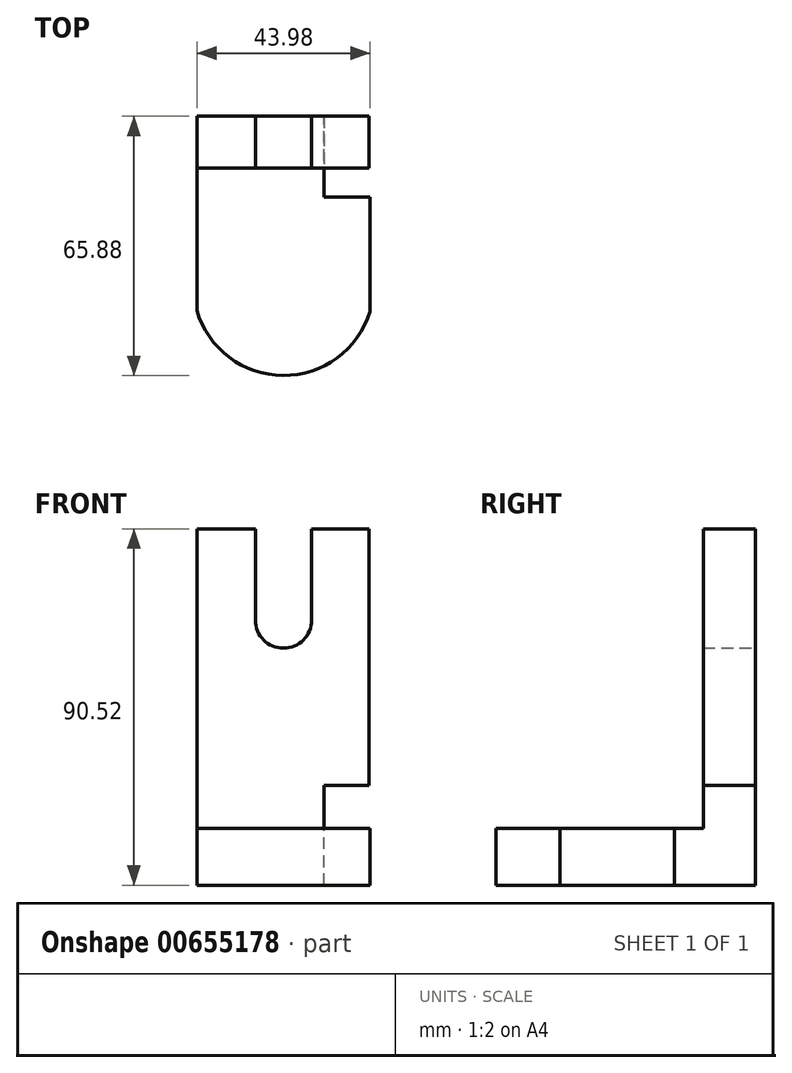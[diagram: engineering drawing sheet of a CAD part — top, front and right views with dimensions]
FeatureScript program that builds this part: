
annotation { "Feature Type Name" : "Feature", "Feature Type Description" : "" }
export const myFeature = defineFeature(function(context is Context, id is Id, definition is map)
    precondition{}
    {
        {
            var Q0;
            Q0=qCreatedBy(makeId("Front.planeOp"),FACE);
            var sketch = newSketch(context, id + "F0", { "sketchPlane" : qUnion([Q0])});
            skLineSegment(sketch, "E0.bottom", {"start": v(-21.85, 45.26) * mm, "end": v(-7, 45.26) * mm});
            skLineSegment(sketch, "E0.top", {"start": v(-21.85, -45.26) * mm, "end": v(21.85, -45.26) * mm});
            skLineSegment(sketch, "E0.left", {"start": v(-21.85, 45.26) * mm, "end": v(-21.85, -45.26) * mm});
            skLineSegment(sketch, "E0.right", {"start": v(21.85, 45.26) * mm, "end": v(21.85, -45.26) * mm});
            skPoint(sketch, "E0.middle", {"position": v(0, 0) * mm});
            skLineSegment(sketch, "E1.left", {"start": v(-7, 45.26) * mm, "end": v(-7, 22.13) * mm});
            skLineSegment(sketch, "E1.right", {"start": v(7.28, 45.26) * mm, "end": v(7.28, 22.13) * mm});
            skArc(sketch, "E2", {"start": v(-7, 22.13) * mm, "mid": v(0.14, 15) * mm, "end": v(7.28, 22.13) * mm});
            skLineSegment(sketch, "E3.trimOffspring", {"start": v(7.28, 45.26) * mm, "end": v(21.85, 45.26) * mm});
            skSolve(sketch);
        }
        {
            var Q0;
            Q0 = qSketchRegion(id + "F0", true);
            extrude(context, id + "F1", {"entities" : qUnion([Q0]), "depth" : 13.2 * mm, "offsetDistance" : 25.4 * mm});
        }
        {
            var Q0;
            Q0=makeQuery(id+"F1.opExtrude","CAP_FACE",FACE,{"disambiguationData":[OSD([sQuery(id+"F0.wireOp",EDGE,"E0.bottom"),sQuery(id+"F0.wireOp",EDGE,"E0.top"),sQuery(id+"F0.wireOp",EDGE,"E0.left"),sQuery(id+"F0.wireOp",EDGE,"E0.right"),sQuery(id+"F0.wireOp",EDGE,"E1.left"),sQuery(id+"F0.wireOp",EDGE,"E1.right"),sQuery(id+"F0.wireOp",EDGE,"E2"),sQuery(id+"F0.wireOp",EDGE,"E3.trimOffspring")])],"isStart":false});
            var sketch = newSketch(context, id + "F2", { "sketchPlane" : qUnion([Q0])});
            skLineSegment(sketch, "E4.bottom", {"start": v(-21.85, -45.26) * mm, "end": v(22.13, -45.26) * mm});
            skLineSegment(sketch, "E4.top", {"start": v(-21.85, -30.86) * mm, "end": v(22.13, -30.86) * mm});
            skLineSegment(sketch, "E4.left", {"start": v(-21.85, -45.26) * mm, "end": v(-21.85, -30.86) * mm});
            skLineSegment(sketch, "E4.right", {"start": v(22.13, -45.26) * mm, "end": v(22.13, -30.86) * mm});
            skSolve(sketch);
        }
        {
            var Q0;
            Q0 = qSketchRegion(id + "F2", true);
            extrude(context, id + "F3", {"entities" : qUnion([Q0]), "operationType" : NewBodyOperationType.ADD, "depth" : 53.85 * mm, "offsetDistance" : 25.4 * mm});
        }
        {
            var Q0;
            Q0=makeQuery(id+"F3.opExtrude","SWEPT_FACE",FACE,{"disambiguationData":[OSD([sQuery(id+"F2.wireOp",EDGE,"E4.top")])]});
            var sketch = newSketch(context, id + "F4", { "sketchPlane" : qUnion([Q0])});
            skArc(sketch, "E5", {"start": v(-21.85, -49.31) * mm, "mid": v(0.03, -65.88) * mm, "end": v(22.13, -49.62) * mm});
            skSolve(sketch);
        }
        {
            var Q0;
            {var subQ0=sQuery(id+"F4.wireOp",EDGE,"E5");Q0=makeQuery(id+"F4.imprint","IMPRINT",FACE,{"disambiguationData":[TD([[makeQuery(id+"F4.imprint","IMPRINT",EDGE,{"derivedFrom":subQ0}),-1.0]])]});}
            extrude(context, id + "F5", {"entities" : qUnion([Q0]), "operationType" : NewBodyOperationType.REMOVE, "oppositeDirection" : true, "depth" : 25.4 * mm, "offsetDistance" : 25.4 * mm});
        }
        {
            var Q0;
            Q0=makeQuery(id+"F3.opExtrude","SWEPT_FACE",FACE,{"disambiguationData":[OSD([sQuery(id+"F2.wireOp",EDGE,"E4.right")])]});
            var sketch = newSketch(context, id + "F6", { "sketchPlane" : qUnion([Q0])});
            skLineSegment(sketch, "E6.bottom", {"start": v(5.2, -52.3) * mm, "end": v(-20.58, -52.3) * mm});
            skLineSegment(sketch, "E6.top", {"start": v(5.2, -19.9) * mm, "end": v(-20.58, -19.9) * mm});
            skLineSegment(sketch, "E6.left", {"start": v(5.2, -52.3) * mm, "end": v(5.2, -19.9) * mm});
            skLineSegment(sketch, "E6.right", {"start": v(-20.58, -52.3) * mm, "end": v(-20.58, -19.9) * mm});
            skSolve(sketch);
        }
        {
            var Q0;
            Q0 = qSketchRegion(id + "F6", true);
            extrude(context, id + "F7", {"entities" : qUnion([Q0]), "operationType" : NewBodyOperationType.REMOVE, "oppositeDirection" : true, "depth" : 11.68 * mm, "offsetDistance" : 25.4 * mm});
        }
    });
